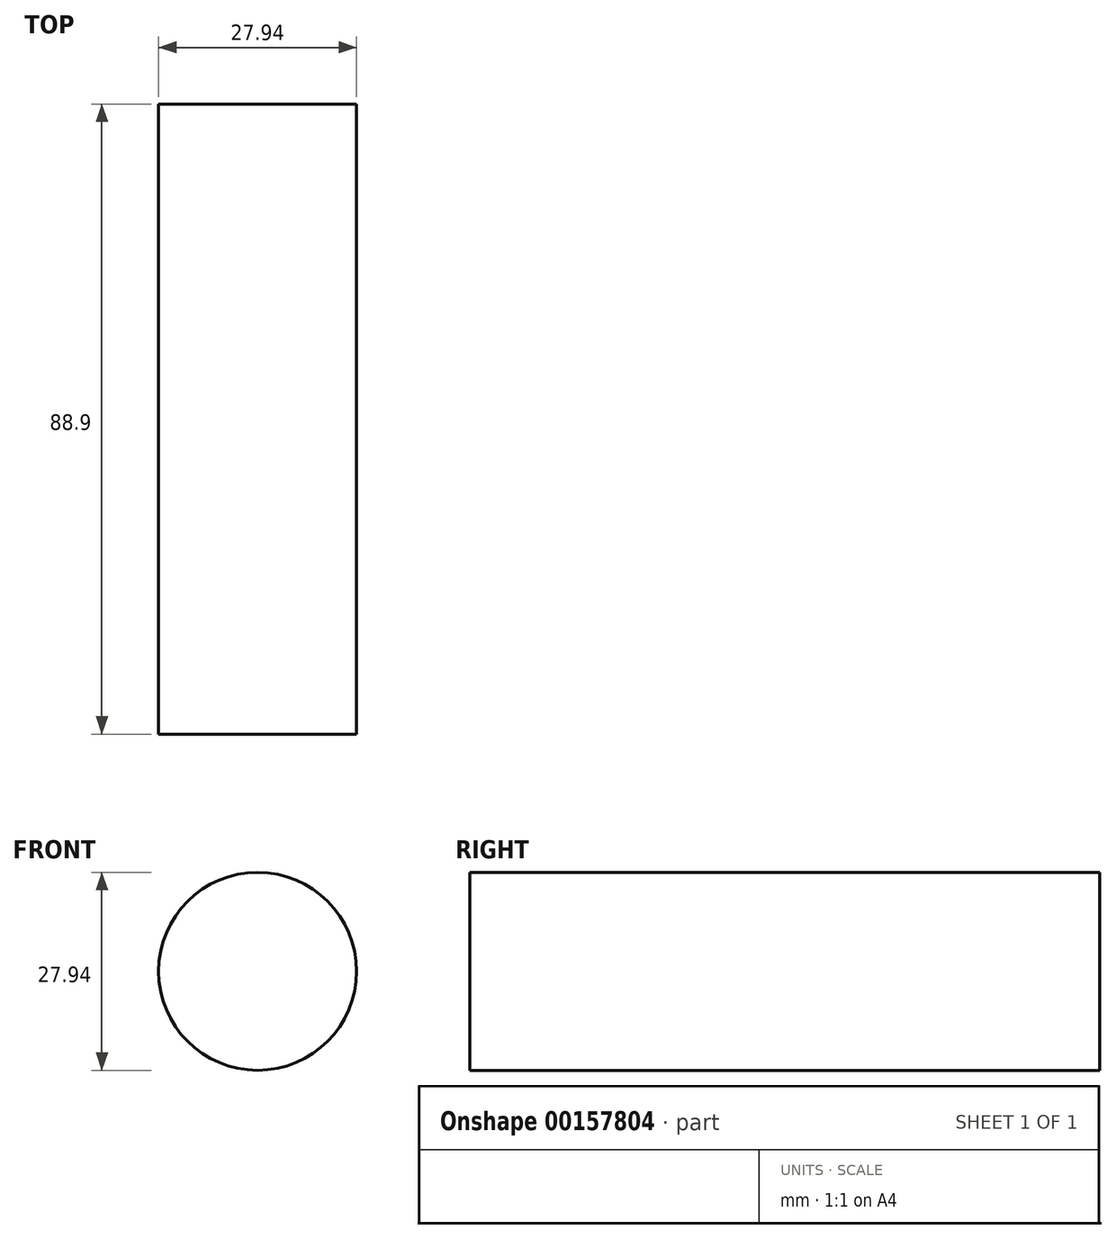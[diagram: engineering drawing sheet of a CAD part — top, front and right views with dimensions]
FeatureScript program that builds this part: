
annotation { "Feature Type Name" : "Feature", "Feature Type Description" : "" }
export const myFeature = defineFeature(function(context is Context, id is Id, definition is map)
    precondition{}
    {
        {
            var Q0;
            Q0=qCreatedBy(makeId("Front.planeOp"),FACE);
            var sketch = newSketch(context, id + "F0", { "sketchPlane" : qUnion([Q0])});
            skCircle(sketch, "E0", {"center": v(0, 0) * mm, "radius": 13.97 * mm});
            skSolve(sketch);
        }
        {
            var Q0;
            Q0=qCreatedBy(makeId("Front.planeOp"),FACE);
            var sketch = newSketch(context, id + "F1", { "sketchPlane" : qUnion([Q0])});
            skCircle(sketch, "E1", {"center": v(0, 0) * mm, "radius": 7.94 * mm});
            skCircle(sketch, "E2", {"center": v(0, 0) * mm, "radius": 1.59 * mm});
            skSolve(sketch);
        }
        {
            var Q0;
            Q0=makeQuery(id+"F0.imprint","IMPRINT",FACE,{"disambiguationData":[TD([[makeQuery(id+"F0.imprint","IMPRINT",EDGE,{"derivedFrom":sQuery(id+"F0.wireOp",EDGE,"E0")}),1.0]])]});
            extrude(context, id + "F2", {"entities" : qUnion([Q0]), "depth" : 88.9 * mm});
        }
        {
            var Q0;
            Q0=makeQuery(id+"F1.imprint","IMPRINT",FACE,{"disambiguationData":[TD([[makeQuery(id+"F1.imprint","IMPRINT",EDGE,{"derivedFrom":sQuery(id+"F1.wireOp",EDGE,"E2")}),1.0]])]});
            var Q1;
            Q1=sQuery(id+"F1.wireOp",EDGE,"E2");
            extrude(context, id + "F3", {"entities" : qUnion([Q0]), "operationType" : NewBodyOperationType.REMOVE, "surfaceEntities" : qUnion([Q1]), "endBound" : BoundingType.THROUGH_ALL, "oppositeDirection" : true, "depth" : 25.4 * mm});
        }
    });
